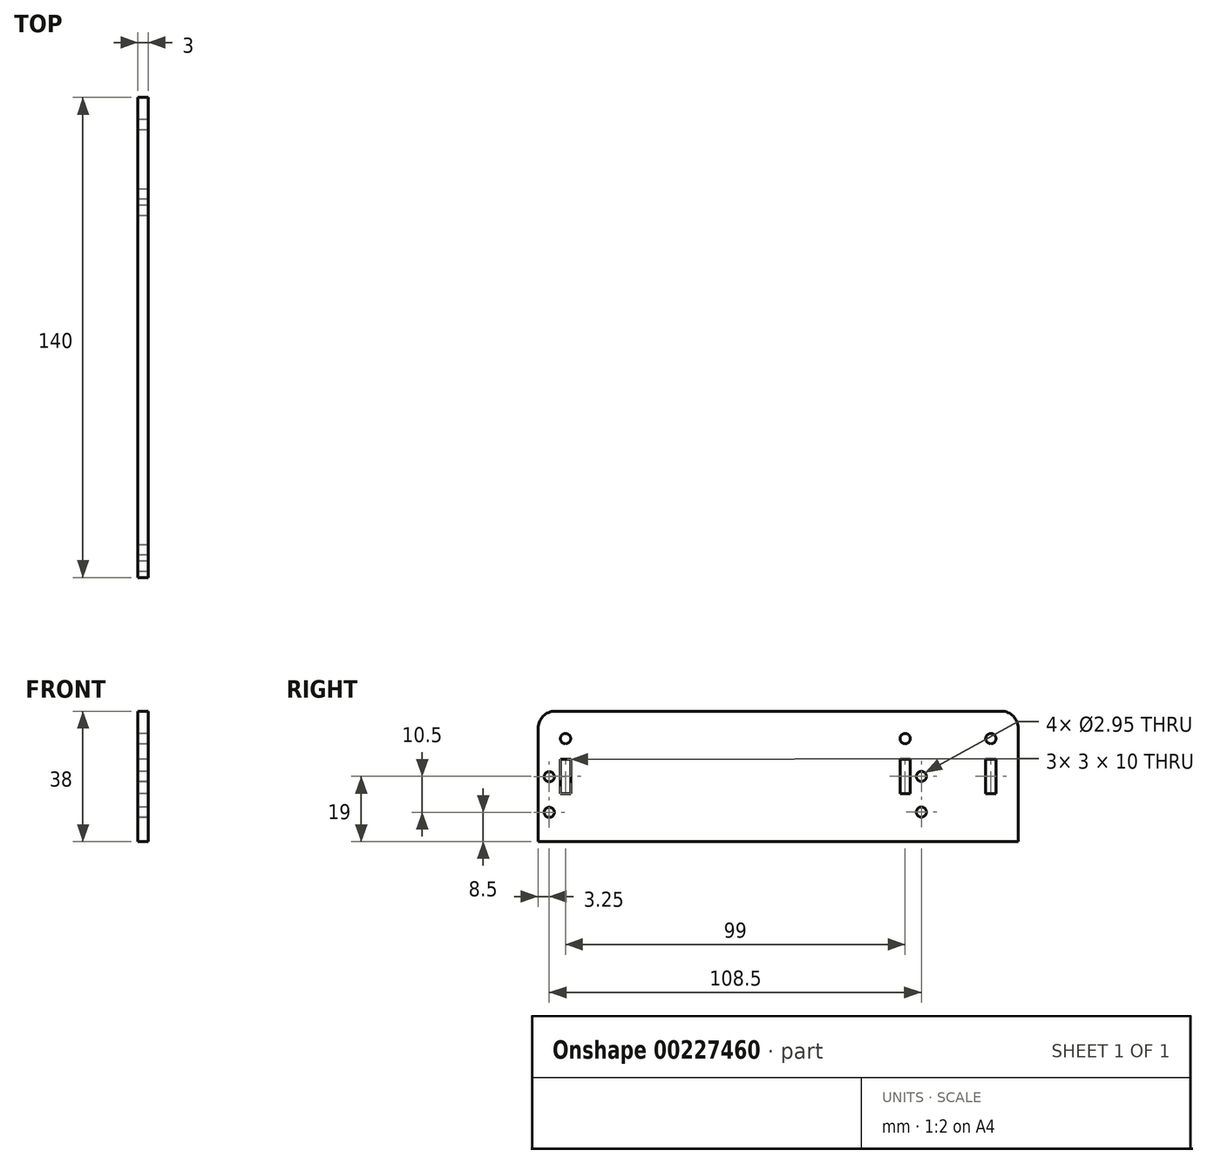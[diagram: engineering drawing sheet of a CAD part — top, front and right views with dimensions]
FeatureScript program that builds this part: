
annotation { "Feature Type Name" : "Feature", "Feature Type Description" : "" }
export const myFeature = defineFeature(function(context is Context, id is Id, definition is map)
    precondition{}
    {
        {
            var Q0;
            Q0=qCreatedBy(makeId("Right.planeOp"),FACE);
            var sketch = newSketch(context, id + "F0", { "sketchPlane" : qUnion([Q0])});
            skLineSegment(sketch, "E0", {"start": v(0, 0) * mm, "end": v(70, 0) * mm});
            skLineSegment(sketch, "E1", {"start": v(70, 0) * mm, "end": v(70, 38) * mm});
            skLineSegment(sketch, "E2", {"start": v(70, 38) * mm, "end": v(35.5, 38) * mm});
            skLineSegment(sketch, "E3", {"start": v(-70, 38) * mm, "end": v(-70, 0) * mm});
            skLineSegment(sketch, "E4", {"start": v(-70, 0) * mm, "end": v(0, 0) * mm});
            skLineSegment(sketch, "E5", {"start": v(37, 38) * mm, "end": v(37, 0) * mm, "construction": true});
            skLineSegment(sketch, "E6", {"start": v(62, 38) * mm, "end": v(62, 0) * mm, "construction": true});
            skLineSegment(sketch, "E7.bottom", {"start": v(60.5, 14) * mm, "end": v(63.5, 14) * mm});
            skLineSegment(sketch, "E7.top", {"start": v(60.5, 24) * mm, "end": v(63.5, 24) * mm});
            skLineSegment(sketch, "E7.left", {"start": v(60.5, 14) * mm, "end": v(60.5, 24) * mm});
            skLineSegment(sketch, "E7.right", {"start": v(63.5, 14) * mm, "end": v(63.5, 24) * mm});
            skPoint(sketch, "E7.middle", {"position": v(62, 19) * mm});
            skLineSegment(sketch, "E8.bottom", {"start": v(35.5, 14) * mm, "end": v(38.5, 14) * mm});
            skLineSegment(sketch, "E8.top", {"start": v(35.5, 24) * mm, "end": v(38.5, 24) * mm});
            skLineSegment(sketch, "E8.left", {"start": v(35.5, 14) * mm, "end": v(35.5, 24) * mm});
            skLineSegment(sketch, "E8.right", {"start": v(38.5, 14) * mm, "end": v(38.5, 24) * mm});
            skPoint(sketch, "E8.middle", {"position": v(37, 19) * mm});
            skLineSegment(sketch, "E9", {"start": v(-62, 0) * mm, "end": v(-62, 38) * mm, "construction": true});
            skLineSegment(sketch, "E10.bottom", {"start": v(-60.5, 14) * mm, "end": v(-63.5, 14) * mm});
            skLineSegment(sketch, "E10.top", {"start": v(-60.5, 24) * mm, "end": v(-63.5, 24) * mm});
            skLineSegment(sketch, "E10.left", {"start": v(-60.5, 14) * mm, "end": v(-60.5, 24) * mm});
            skLineSegment(sketch, "E10.right", {"start": v(-63.5, 14) * mm, "end": v(-63.5, 24) * mm});
            skPoint(sketch, "E10.middle", {"position": v(-62, 19) * mm});
            skPoint(sketch, "E11", {"position": v(62, 30) * mm});
            skCircle(sketch, "E12", {"center": v(62, 30) * mm, "radius": 1.5 * mm});
            skPoint(sketch, "E13", {"position": v(37, 30) * mm});
            skCircle(sketch, "E14", {"center": v(37, 30) * mm, "radius": 1.5 * mm});
            skPoint(sketch, "E15", {"position": v(-62, 30) * mm});
            skCircle(sketch, "E16", {"center": v(-62, 30) * mm, "radius": 1.5 * mm});
            skLineSegment(sketch, "E17", {"start": v(35.5, 38) * mm, "end": v(-70, 38) * mm});
            skPoint(sketch, "E18", {"position": v(-66.75, 8.5) * mm});
            skPoint(sketch, "E19", {"position": v(-66.75, 18.9) * mm});
            skCircle(sketch, "E20", {"center": v(-66.75, 8.5) * mm, "radius": 1.48 * mm});
            skCircle(sketch, "E21", {"center": v(-66.75, 18.9) * mm, "radius": 1.48 * mm});
            skPoint(sketch, "E22", {"position": v(41.75, 19) * mm});
            skPoint(sketch, "E23", {"position": v(41.75, 8.6) * mm});
            skCircle(sketch, "E24", {"center": v(41.75, 19) * mm, "radius": 1.48 * mm});
            skCircle(sketch, "E25", {"center": v(41.75, 8.6) * mm, "radius": 1.48 * mm});
            skSolve(sketch);
        }
        {
            var Q0;
            Q0=makeQuery(id+"F0.imprint","IMPRINT",FACE,{"disambiguationData":[TD([[makeQuery(id+"F0.imprint","IMPRINT",EDGE,{"derivedFrom":sQuery(id+"F0.wireOp",EDGE,"E0")}),1.0]])]});
            extrude(context, id + "F1", {"entities" : qUnion([Q0]), "depth" : 3 * mm});
        }
        {
            var Q0;
            Q0=makeQuery(id+"F1.opExtrude","SWEPT_EDGE",EDGE,{"disambiguationData":[OSD([sQuery(id+"F0.wireOp",EDGE,"E1"),sQuery(id+"F0.wireOp",EDGE,"E2")])]});
            var Q1;
            Q1=makeQuery(id+"F1.opExtrude","SWEPT_EDGE",EDGE,{"disambiguationData":[OSD([sQuery(id+"F0.wireOp",EDGE,"E3"),sQuery(id+"F0.wireOp",EDGE,"E17")])]});
            fillet(context, id + "F2", {"entities" : qUnion([Q0, Q1]), "radius" : 5 * mm, "tangentPropagation" : true, "allowEdgeOverflow" : false});
        }
    });
